# Revit family: Toilet-Wall_Mount-KOHLER-MODERN_LIFE-K-77142IN
name_source: partatom
category: Plumbing Fixtures
revit_build: Autodesk Revit 2017 (Build: 20160225_1515(x64)
units: mm (PartAtom-declared; Revit-internal decimal feet)

## family parameters
Cut with Voids When Loaded = No
Host = Face
OmniClass Number = 23.31.19.00
OmniClass Title = Toilets
Part Type = Normal
Room Calculation Point = No
Round Connector Dimension = Use Diameter
Shared = No

## types (5) — shared parameters
ADA Compliant = No
Assembly Code = D2010100
CW Connection = Yes
Cold Water Inlet = Cold Water Inlet
Date Modified = 01/20/2021
Default Elevation = 0"
Description = WH TOILET WITH QC UF SEAT
Flow Rate = 0 GPM
Flush Rate- GPF = GPF
Flush Rate- LPF = LPF
HW Connection = No
Height = 13 13/16"
Hot Water Inlet = Hot Water Inlet
Length = 21 1/4"
Manufacturer = KOHLER Co.
Master Format 2014 = 22 42 13.13
Master Format 2014 Name = Residential Water Closets
Material = Viterious China
Pressure = 0.00 psi
Product Name = MODERN LIFE
Seat Included = Yes
URL = https://www.kohler.co.in
Vent Connection = No
Waste Connection = Yes
Waste Water Outlet = Waste Water Outlet
WaterSense Certified = No
Width = 14 3/16"

## per-type parameters (varying)
| type | Finish | Model | Product Page URL | Type |
| SS, 0- White | Kohler-Vitreous_China-0-White | K-77142IN-SS-0 |  | 1 |
| S, 0-White | Kohler-Vitreous_China-0-White | K-77142IN-S-0 | https://www.kohler.co.in | 2 |
| S, HG1- Thunder Grey | Kohler-Vitreous_China-HG1-Honed_Thunder_Grey | K-77142IN-S-HG1 | https://www.kohler.co.in | 3 |
| S, HP1- Peacock | Kohler-Vitreous_China-HP1-Honed_Peacock | K-77142IN-S-HP1 | https://www.kohler.co.in | 4 |
| S, HT1- Truffle | Kohler-Vitreous_China-HT1-Honed_Truffle | K-77142IN-S-HT1 | https://www.kohler.co.in | 5 |

## geometry (parser evidence)
native form markers: Sweep x5
no freeform markers — native parametric forms only
